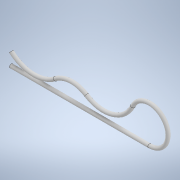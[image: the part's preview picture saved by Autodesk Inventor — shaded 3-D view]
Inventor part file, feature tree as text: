
AUTODESK INVENTOR PART (.ipt)
format: ipt  version: 2022 (Build 260153000, 153)  size: 140,288 bytes
history: native  units: mm
features: sketch x2, sweep x1
ambient origin geometry x8: Origin, YZ Plane, XZ Plane, XY Plane, X Axis, Y Axis, Z Axis, Center Point
bodies: Solid1 (feature_tree)
feature tree (3):
  sweep  "Sweep1"
  sketch  "Sketch2"  dims[d2=2.0mm d3=90.0deg]
  sketch  "Sketch3"  dims[d4=75.0mm d6=2.0mm d7=0.0mm d8=0.0mm d9=10.0mm d10=4.0mm]
